FCSTD DOCUMENT  (FreeCAD 0.19R24291 (Git))
Label: ferris_wheel
License: All rights reserved
LicenseURL: http://en.wikipedia.org/wiki/All_rights_reserved
objects: Sketcher::SketchObject×4, PartDesign::Body×3
note: 7 computed .brp shape members not serialized (recipe doc carries the construction recipe); baked Part::Feature solids carry a one-line shape summary decoded from their .brp

FEATURE [Sketcher::SketchObject] Sketch
  FullyConstrained = false
  MapMode = 5
  Placement = pos=(0,0,0) rot=(0.57735,0.57735,0.57735;2.0944rad)
  Support = -> [YZ_Plane]
  sketch-geometry (6):
    g0: ArcOfCircle CenterX=0 CenterY=0 CenterZ=0 NormalX=0 NormalY=0 NormalZ=1 AngleXU=0 Radius=43.864 StartAngle=4.71239 EndAngle=7.85398
    g1: ArcOfCircle CenterX=0 CenterY=0 CenterZ=0 NormalX=0 NormalY=0 NormalZ=1 AngleXU=0 Radius=68.4818 StartAngle=0.359448 EndAngle=1.5708
    g2: LineSegment StartX=64.1052 StartY=24.089 StartZ=0 EndX=120.79 EndY=-126.76 EndZ=0
    g3: LineSegment StartX=120.79 StartY=-126.76 StartZ=0 EndX=0 EndY=-126.76 EndZ=0
    g4: LineSegment StartX=1.34e-14 StartY=43.864 StartZ=0 EndX=4.2e-15 EndY=68.4818 EndZ=0
    g5: LineSegment StartX=-8.1e-15 StartY=-43.864 StartZ=0 EndX=0 EndY=-126.76 EndZ=0
  constraints (14):
    c: Coincident(g0,g-1)
    c: PointOnObject(g0,g-2)
    c: PointOnObject(g0,g-2)
    c: Coincident(g1,g0)
    c: PointOnObject(g1,g-2)
    c: Coincident(g2,g1)
    c: Coincident(g3,g2)
    c: PointOnObject(g3,g-2)
    c: Horizontal(g3)
    c: Tangent(g1,g2)
    c: Coincident(g4,g0)
    c: Coincident(g4,g1)
    c: Coincident(g5,g0)
    c: Coincident(g5,g3)
FEATURE [Sketcher::SketchObject] Sketch001
  FullyConstrained = false
  MapMode = 5
  Placement = pos=(0,0,0) rot=(0.57735,0.57735,0.57735;2.0944rad)
  Support = -> [YZ_Plane]
  sketch-geometry (6):
    g0: LineSegment StartX=0 StartY=-109.492 StartZ=0 EndX=104.133 EndY=-33.835 EndZ=0
    g1: LineSegment StartX=104.133 StartY=-33.835 StartZ=0 EndX=64.3579 EndY=88.5811 EndZ=0
    g2: LineSegment StartX=64.3579 StartY=88.5811 StartZ=0 EndX=-64.3579 EndY=88.5811 EndZ=0
    g3: LineSegment StartX=-64.3579 StartY=88.5811 StartZ=0 EndX=-104.133 EndY=-33.835 EndZ=0
    g4: LineSegment StartX=-104.133 StartY=-33.835 StartZ=0 EndX=0 EndY=-109.492 EndZ=0
    g5: Circle CenterX=0 CenterY=0 CenterZ=0 NormalX=0 NormalY=0 NormalZ=1 AngleXU=0 Radius=109.492
  constraints (13):
    c: Coincident(g0,g1)
    c: Coincident(g1,g2)
    c: Coincident(g2,g3)
    c: Coincident(g3,g4)
    c: Coincident(g4,g0)
    c: Equal(g0, g1-g4) x4
    c: PointOnObject(g0,g5)
    c: PointOnObject(g1,g5)
    c: PointOnObject(g2,g5)
    c: PointOnObject(g3,g5)
    c: PointOnObject(g4,g5)
    c: Coincident(g5,g-1)
    c: PointOnObject(g4,g-2)
FEATURE [PartDesign::Body] Body
  Group = -> [Sketch,Sketch001]
  Origin = -> Origin
FEATURE [Sketcher::SketchObject] Sketch002
  FullyConstrained = false
  MapMode = 5
  Placement = pos=(0,0,0) rot=(0.57735,0.57735,0.57735;2.0944rad)
  Support = -> [YZ_Plane001]
  sketch-geometry (21):
    g0: LineSegment StartX=0 StartY=-116.132 StartZ=0 EndX=110.448 EndY=-35.8867 EndZ=0
    g1: LineSegment StartX=110.448 StartY=-35.8867 StartZ=0 EndX=68.2605 EndY=93.9525 EndZ=0
    g2: LineSegment StartX=68.2605 StartY=93.9525 StartZ=0 EndX=-68.2605 EndY=93.9525 EndZ=0
    g3: LineSegment StartX=-68.2605 StartY=93.9525 StartZ=0 EndX=-110.448 EndY=-35.8867 EndZ=0
    g4: LineSegment StartX=-110.448 StartY=-35.8867 StartZ=0 EndX=0 EndY=-116.132 EndZ=0
    g5: Circle CenterX=0 CenterY=0 CenterZ=0 NormalX=0 NormalY=0 NormalZ=1 AngleXU=0 Radius=116.132
    g6: LineSegment StartX=15.9152 StartY=20.5742 StartZ=0 EndX=68.2605 EndY=93.9525 EndZ=0
    g7: ArcOfCircle CenterX=0 CenterY=0 CenterZ=0 NormalX=0 NormalY=0 NormalZ=1 AngleXU=0 Radius=26.0114 StartAngle=0.912394 EndAngle=1.5708
    g8: LineSegment StartX=68.2605 StartY=93.9525 StartZ=0 EndX=43.6932 EndY=93.9525 EndZ=0
    g9: ArcOfCircle CenterX=0 CenterY=125.122 CenterZ=0 NormalX=0 NormalY=0 NormalZ=1 AngleXU=0 Radius=53.6713 StartAngle=4.71239 EndAngle=5.66355
    g10: LineSegment StartX=43.6932 StartY=93.9525 StartZ=0 EndX=43.8254 EndY=94.1379 EndZ=0
    g11: LineSegment StartX=-9.9e-15 StartY=71.4504 StartZ=0 EndX=-1.8e-15 EndY=65.0513 EndZ=0
    g12: ArcOfCircle CenterX=0 CenterY=125.122 CenterZ=0 NormalX=0 NormalY=0 NormalZ=1 AngleXU=0 Radius=73.6713 StartAngle=4.71239 EndAngle=4.90892
    g13: LineSegment StartX=14.3853 StartY=52.8685 StartZ=0 EndX=4.52418 EndY=39.045 EndZ=0
    g14: ArcOfCircle CenterX=0 CenterY=0 CenterZ=0 NormalX=0 NormalY=0 NormalZ=1 AngleXU=0 Radius=39.3063 StartAngle=1.45544 EndAngle=1.5708
    g15: LineSegment StartX=43.6932 StartY=93.9525 StartZ=0 EndX=59.9749 EndY=82.3377 EndZ=0
    g16: LineSegment StartX=14.3853 StartY=52.8685 StartZ=0 EndX=30.6671 EndY=41.2537 EndZ=0
    g17: Circle CenterX=13.3105 CenterY=32.9931 CenterZ=0 NormalX=0 NormalY=0 NormalZ=1 AngleXU=0 Radius=1.86797
    g18: ArcOfCircle CenterX=-2.6e-15 CenterY=62.2646 CenterZ=0 NormalX=0 NormalY=0 NormalZ=1 AngleXU=0 Radius=2.78675 StartAngle=4.71239 EndAngle=7.85398
    g19: LineSegment StartX=-3.1e-15 StartY=59.4778 StartZ=0 EndX=-1.35e-14 EndY=51.4504 EndZ=0
    g20: LineSegment StartX=1.6e-15 StartY=26.0114 StartZ=0 EndX=2.4e-15 EndY=39.3063 EndZ=0
  constraints (48):
    c: Coincident(g0,g1)
    c: Coincident(g1,g2)
    c: Coincident(g2,g3)
    c: Coincident(g3,g4)
    c: Coincident(g4,g0)
    c: Equal(g0, g1-g4) x4
    c: PointOnObject(g0,g5)
    c: PointOnObject(g1,g5)
    c: PointOnObject(g2,g5)
    c: PointOnObject(g3,g5)
    c: PointOnObject(g4,g5)
    c: Coincident(g5,g-1)
    c: PointOnObject(g4,g-2)
    c: Coincident(g6,g1)
    c: Coincident(g7,g-1)
    c: Coincident(g7,g6)
    c: PointOnObject(g7,g-2)
    c: Coincident(g8,g6)
    c: PointOnObject(g8,g2)
    c: PointOnObject(g9,g-2)
    c: Coincident(g9,g8)
    c: PointOnObject(g9,g-2)
    c: Coincident(g10,g8)
    c: Parallel(g10,g6)
    c: Tangent(g10,g9)
    c: Coincident(g11,g9)
    c: PointOnObject(g19,g-2)
    c: Coincident(g12,g9)
    c: Coincident(g12,g19)
    c: Coincident(g13,g12)
    c: Coincident(g14,g7)
    c: Coincident(g14,g13)
    c: PointOnObject(g14,g-2)
    c: Parallel(g13,g6)
    c: Coincident(g15,g8)
    c: PointOnObject(g15,g6)
    c: Perpendicular(g6,g15)
    c: Distance(g15) = 20
    c: Coincident(g16,g12)
    c: PointOnObject(g16,g6)
    c: Equal(g15,g16)
    c: Perpendicular(g6,g16)
    c: PointOnObject(g18,g11)
    c: Coincident(g11,g18)
    c: Coincident(g19,g18)
    c: Tangent(g11,g19)
    c: Coincident(g20,g7)
    c: Coincident(g20,g14)
FEATURE [PartDesign::Body] Body001
  Group = -> [Sketch002]
  Origin = -> Origin001
FEATURE [Sketcher::SketchObject] Sketch003
  FullyConstrained = false
  MapMode = 5
  Support = -> [XY_Plane002]
  sketch-geometry (1):
    g0: ArcOfCircle CenterX=0 CenterY=0 CenterZ=0 NormalX=0 NormalY=0 NormalZ=1 AngleXU=0 Radius=33.9348 StartAngle=0 EndAngle=0.26219
  constraints (2):
    c: Coincident(g0,g-1)
    c: PointOnObject(g0,g-1)
FEATURE [PartDesign::Body] Body002
  Group = -> [Sketch003]
  Origin = -> Origin002
